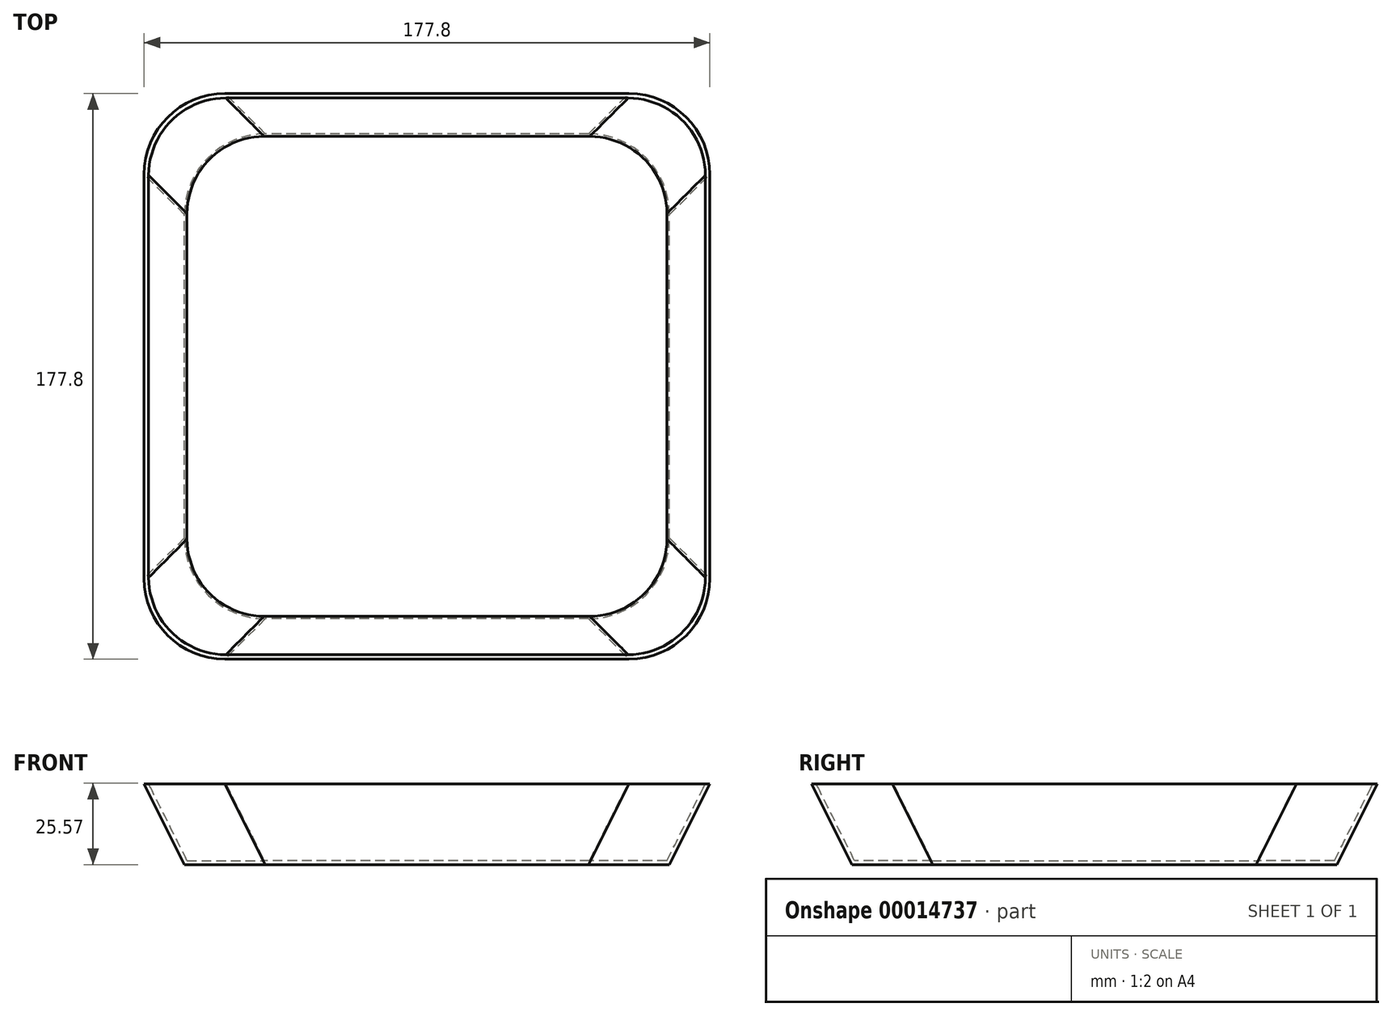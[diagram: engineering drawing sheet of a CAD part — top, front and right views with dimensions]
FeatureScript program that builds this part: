
annotation { "Feature Type Name" : "Feature", "Feature Type Description" : "" }
export const myFeature = defineFeature(function(context is Context, id is Id, definition is map)
    precondition{}
    {
        {
            var Q0;
            Q0=qCreatedBy(makeId("Top.planeOp"),FACE);
            var sketch = newSketch(context, id + "F0", { "sketchPlane" : qUnion([Q0])});
            skLineSegment(sketch, "E0.rect.bottom", {"start": v(50.8, -76.2) * mm, "end": v(-50.8, -76.2) * mm});
            skLineSegment(sketch, "E0.rect.top", {"start": v(50.8, 76.2) * mm, "end": v(-50.8, 76.2) * mm});
            skLineSegment(sketch, "E0.rect.left", {"start": v(76.2, -50.8) * mm, "end": v(76.2, 50.8) * mm});
            skLineSegment(sketch, "E0.rect.right", {"start": v(-76.2, -50.8) * mm, "end": v(-76.2, 50.8) * mm});
            skPoint(sketch, "E0.rect.middle", {"position": v(0, 0) * mm});
            skPoint(sketch, "E1.visualSharp", {"position": v(-76.2, 76.2) * mm});
            skArc(sketch, "E1.filletArc", {"start": v(-50.8, 76.2) * mm, "mid": v(-68.76, 68.76) * mm, "end": v(-76.2, 50.8) * mm});
            skPoint(sketch, "E2.visualSharp", {"position": v(-76.2, -76.2) * mm});
            skArc(sketch, "E2.filletArc", {"start": v(-76.2, -50.8) * mm, "mid": v(-68.76, -68.76) * mm, "end": v(-50.8, -76.2) * mm});
            skPoint(sketch, "E3.visualSharp", {"position": v(76.2, -76.2) * mm});
            skArc(sketch, "E3.filletArc", {"start": v(50.8, -76.2) * mm, "mid": v(68.76, -68.76) * mm, "end": v(76.2, -50.8) * mm});
            skPoint(sketch, "E4.visualSharp", {"position": v(76.2, 76.2) * mm});
            skArc(sketch, "E4.filletArc", {"start": v(76.2, 50.8) * mm, "mid": v(68.76, 68.76) * mm, "end": v(50.8, 76.2) * mm});
            skSolve(sketch);
        }
        {
            var Q0;
            Q0=qCreatedBy(makeId("Top.planeOp"),FACE);
            cPlane(context, id + "F1", {"entities" : qUnion([Q0]), "cplaneType" : CPlaneType.OFFSET, "offset" : 25.4 * mm, "width" : 152.4 * mm, "height" : 152.4 * mm});
        }
        {
            var Q0;
            Q0=qCreatedBy(id+"F1.planeOp",FACE);
            var sketch = newSketch(context, id + "F2", { "sketchPlane" : qUnion([Q0])});
            skLineSegment(sketch, "E5.rect.bottom", {"start": v(-63.5, 88.9) * mm, "end": v(63.5, 88.9) * mm});
            skLineSegment(sketch, "E5.rect.top", {"start": v(-63.5, -88.9) * mm, "end": v(63.5, -88.9) * mm});
            skLineSegment(sketch, "E5.rect.left", {"start": v(-88.9, 63.5) * mm, "end": v(-88.9, -63.5) * mm});
            skLineSegment(sketch, "E5.rect.right", {"start": v(88.9, 63.5) * mm, "end": v(88.9, -63.5) * mm});
            skPoint(sketch, "E5.rect.middle", {"position": v(0, 0) * mm});
            skPoint(sketch, "E6.visualSharp", {"position": v(-88.9, 88.9) * mm});
            skArc(sketch, "E6.filletArc", {"start": v(-63.5, 88.9) * mm, "mid": v(-81.46, 81.46) * mm, "end": v(-88.9, 63.5) * mm});
            skPoint(sketch, "E7.visualSharp", {"position": v(88.9, 88.9) * mm});
            skArc(sketch, "E7.filletArc", {"start": v(88.9, 63.5) * mm, "mid": v(81.46, 81.46) * mm, "end": v(63.5, 88.9) * mm});
            skPoint(sketch, "E8.visualSharp", {"position": v(88.9, -88.9) * mm});
            skArc(sketch, "E8.filletArc", {"start": v(63.5, -88.9) * mm, "mid": v(81.46, -81.46) * mm, "end": v(88.9, -63.5) * mm});
            skPoint(sketch, "E9.visualSharp", {"position": v(-88.9, -88.9) * mm});
            skArc(sketch, "E9.filletArc", {"start": v(-88.9, -63.5) * mm, "mid": v(-81.46, -81.46) * mm, "end": v(-63.5, -88.9) * mm});
            skSolve(sketch);
        }
        {
            var Q0;
            Q0=makeQuery(id+"F0.imprint","IMPRINT",FACE,{"disambiguationData":[TD([[makeQuery(id+"F0.imprint","IMPRINT",EDGE,{"derivedFrom":sQuery(id+"F0.wireOp",EDGE,"E0.rect.bottom")}),-1.0]])]});
            var Q1;
            Q1=makeQuery(id+"F2.imprint","IMPRINT",FACE,{"disambiguationData":[TD([[makeQuery(id+"F2.imprint","IMPRINT",EDGE,{"derivedFrom":sQuery(id+"F2.wireOp",EDGE,"E5.rect.bottom")}),-1.0]])]});
            loft(context, id + "F3", {"sheetProfilesArray" : [{ "sheetProfileEntities" : qUnion([Q0]) }, { "sheetProfileEntities" : qUnion([Q1]) }]});
        }
        {
            var Q0;
            Q0=makeQuery(id+"F3.opLoft","CAP_FACE",FACE,{"disambiguationData":[OSD([makeQuery(id+"F2.imprint","IMPRINT",FACE,{"disambiguationData":[TD([[makeQuery(id+"F2.imprint","IMPRINT",EDGE,{"derivedFrom":sQuery(id+"F2.wireOp",EDGE,"E5.rect.bottom")}),-1.0]])]})])],"isStart":true});
            shell(context, id + "F4", {"entities" : qUnion([Q0]), "thickness" : 1.27 * mm});
        }
    });
